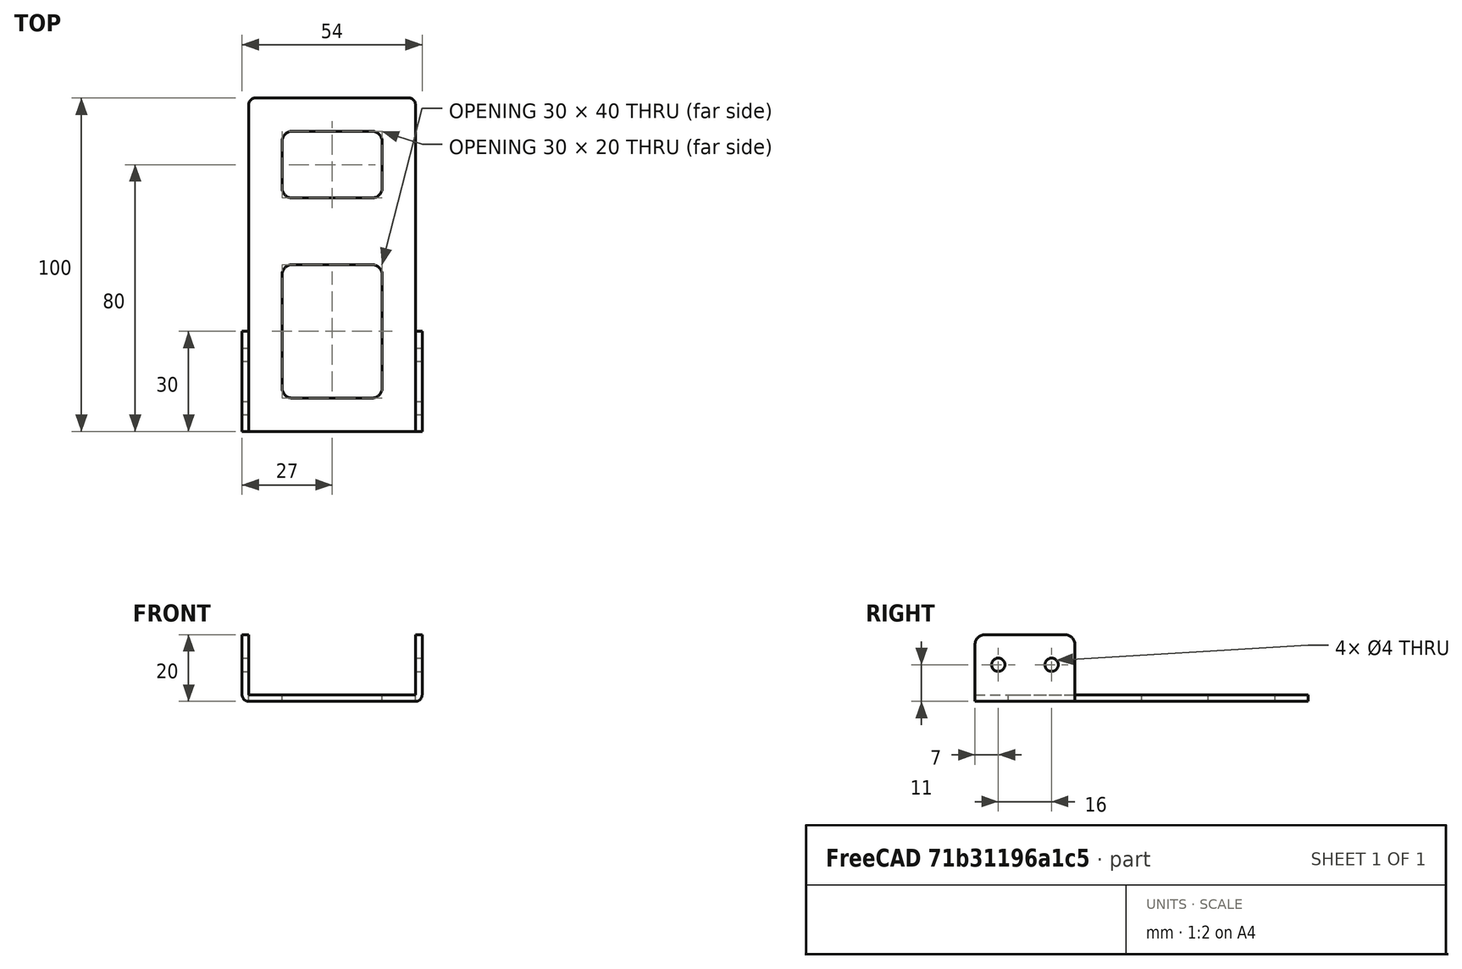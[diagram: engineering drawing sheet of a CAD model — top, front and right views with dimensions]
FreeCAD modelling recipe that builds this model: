
FCSTD DOCUMENT  (FreeCAD 0.18.4R)
Label: tutorial_freecad_ex12_d
License: All rights reserved
LicenseURL: http://en.wikipedia.org/wiki/All_rights_reserved
objects: Part::Box×5, Part::Fillet×5, Part::MultiFuse×4, Part::Cylinder×4, Part::Cut×3
note: 21 computed .brp shape members not serialized (recipe doc carries the construction recipe); baked Part::Feature solids carry a one-line shape summary decoded from their .brp

FEATURE [Part::Box] Box  label="base"
  AttacherType = Attacher::AttachEngine3D
  Height = 2
  Length = 50
  Width = 100
FEATURE [Part::Box] Box001  label="hueco_superior_30x20"
  AttacherType = Attacher::AttachEngine3D
  Height = 2.4
  Length = 30
  Placement = pos=(10,70,-0.2) rot=(0,0,1;0rad)
  Width = 20
FEATURE [Part::Box] Box002  label="hueco_inferior_40x30"
  AttacherType = Attacher::AttachEngine3D
  Height = 2.4
  Length = 30
  Placement = pos=(10,10,-0.2) rot=(0,0,1;0rad)
  Width = 40
FEATURE [Part::MultiFuse] Fusion  label="huecos_base"
  Refine = true
  Shapes = -> [Box001,Box002]
FEATURE [Part::Cut] Cut  label="base_perforada"
  Base = -> Box
  Refine = true
  Tool = -> Fusion
FEATURE [Part::Box] Box003  label="ala"
  AttacherType = Attacher::AttachEngine3D
  Height = 20
  Length = 2
  Placement = pos=(-2,0,0) rot=(0,0,1;0rad)
  Width = 30
FEATURE [Part::Cylinder] Cylinder  label="hueco_tornillo_01"
  Angle = 360
  AttacherType = Attacher::AttachEngine3D
  Height = 4
  Placement = pos=(-3,7,11) rot=(0,1,0;1.5708rad)
  Radius = 2
FEATURE [Part::Cylinder] Cylinder001  label="hueco_tornillo_02"
  Angle = 360
  AttacherType = Attacher::AttachEngine3D
  Height = 4
  Placement = pos=(-3,23,11) rot=(0,1,0;1.5708rad)
  Radius = 2
FEATURE [Part::MultiFuse] Fusion001
  Refine = true
  Shapes = -> [Cylinder,Cylinder001]
FEATURE [Part::Cut] Cut001  label="ala_izquierda"
  Base = -> Box003
  Refine = true
  Tool = -> Fusion001
FEATURE [Part::Fillet] Fillet  label="ala_izquierda_redondeada"
  Base = -> Cut001
  Edges = 2 edges r=3: [Edge9,Edge10]
FEATURE [Part::Box] Box004  label="ala001"
  AttacherType = Attacher::AttachEngine3D
  Height = 20
  Length = 2
  Placement = pos=(-2,0,0) rot=(0,0,1;0rad)
  Width = 30
FEATURE [Part::Cylinder] Cylinder002  label="hueco_tornillo_003"
  Angle = 360
  AttacherType = Attacher::AttachEngine3D
  Height = 4
  Placement = pos=(-3,7,11) rot=(0,1,0;1.5708rad)
  Radius = 2
FEATURE [Part::Cylinder] Cylinder003  label="hueco_tornillo_004"
  Angle = 360
  AttacherType = Attacher::AttachEngine3D
  Height = 4
  Placement = pos=(-3,23,11) rot=(0,1,0;1.5708rad)
  Radius = 2
FEATURE [Part::MultiFuse] Fusion002
  Refine = true
  Shapes = -> [Cylinder002,Cylinder003]
FEATURE [Part::Cut] Cut002  label="ala_izquierda001"
  Base = -> Box004
  Refine = true
  Tool = -> Fusion002
FEATURE [Part::Fillet] Fillet001  label="ala_derecha_redondeada"
  Base = -> Cut002
  Edges = 2 edges r=3: [Edge9,Edge10]
  Placement = pos=(52,0,0) rot=(0,0,1;0rad)
FEATURE [Part::Fillet] Fillet002  label="base_perforada_redondeo_interno_3mm"
  Base = -> Cut
  Edges = 8 edges r=3: [Edge29,Edge30,Edge31,Edge32,Edge33,Edge34,Edge35,Edge36]
FEATURE [Part::Fillet] Fillet003  label="base_perforada_redondeada_externo_2mm"
  Base = -> Fillet002
  Edges = 2 edges r=2: [Edge38,Edge41]
FEATURE [Part::MultiFuse] Fusion003
  Refine = true
  Shapes = -> [Fillet001,Fillet,Fillet003]
FEATURE [Part::Fillet] Fillet004  label="pieza_final"
  Base = -> Fusion003
  Edges = 2 edges r=2: [Edge47,Edge111]
